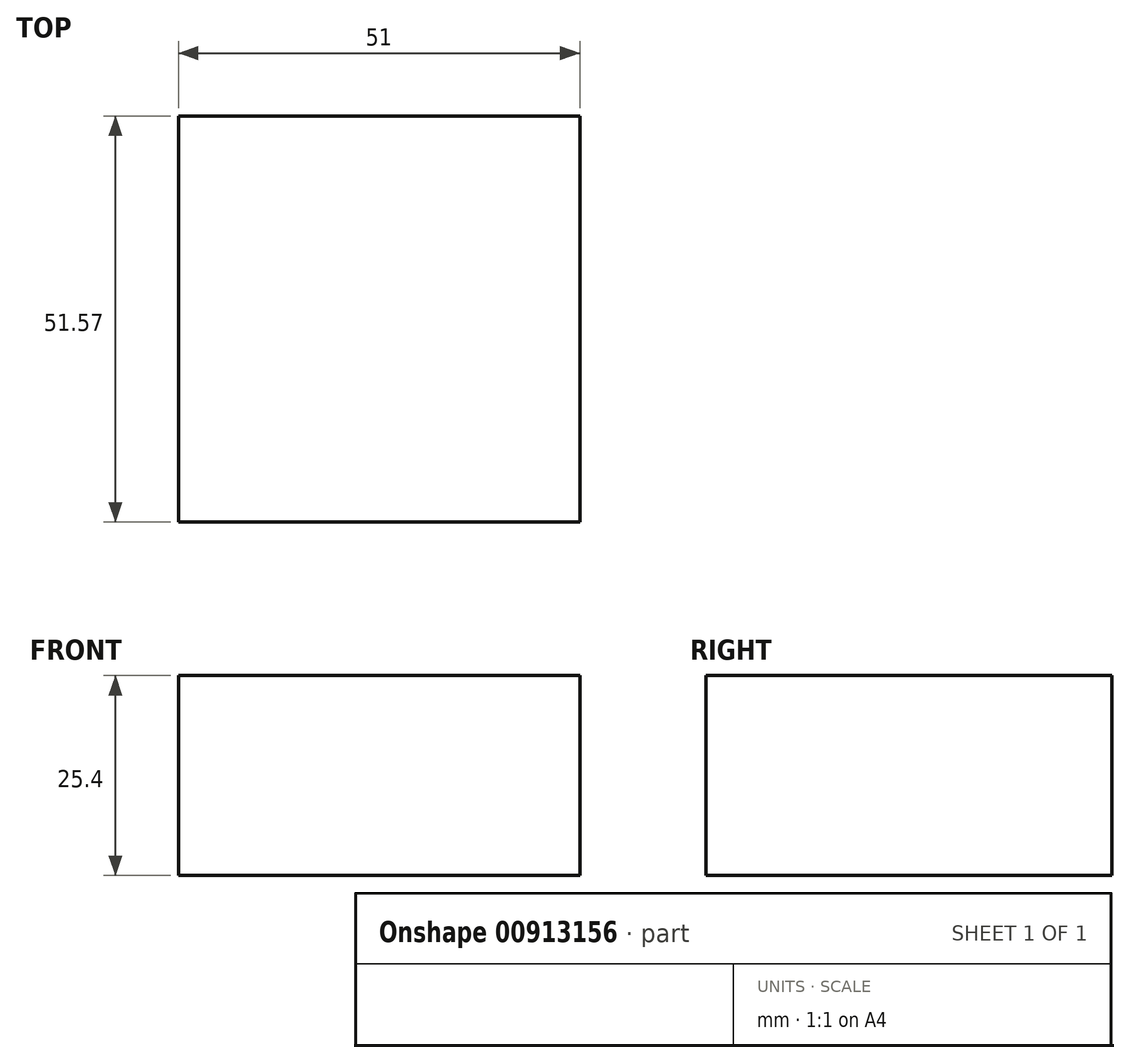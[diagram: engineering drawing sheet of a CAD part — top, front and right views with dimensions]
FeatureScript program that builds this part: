
annotation { "Feature Type Name" : "Feature", "Feature Type Description" : "" }
export const myFeature = defineFeature(function(context is Context, id is Id, definition is map)
    precondition{}
    {
        {
            var Q0;
            Q0=qCreatedBy(makeId("Top.planeOp"),FACE);
            var sketch = newSketch(context, id + "F0", { "sketchPlane" : qUnion([Q0])});
            skLineSegment(sketch, "E0.bottom", {"start": v(-22.09, -25.7) * mm, "end": v(28.91, -25.7) * mm});
            skLineSegment(sketch, "E0.top", {"start": v(-22.09, 25.88) * mm, "end": v(28.91, 25.88) * mm});
            skLineSegment(sketch, "E0.left", {"start": v(-22.09, -25.7) * mm, "end": v(-22.09, 25.88) * mm});
            skLineSegment(sketch, "E0.right", {"start": v(28.91, -25.7) * mm, "end": v(28.91, 25.88) * mm});
            skSolve(sketch);
        }
        {
            var Q0;
            Q0 = qSketchRegion(id + "F0", true);
            extrude(context, id + "F1", {"entities" : qUnion([Q0]), "depth" : 25.4 * mm, "offsetDistance" : 25.4 * mm});
        }
    });
